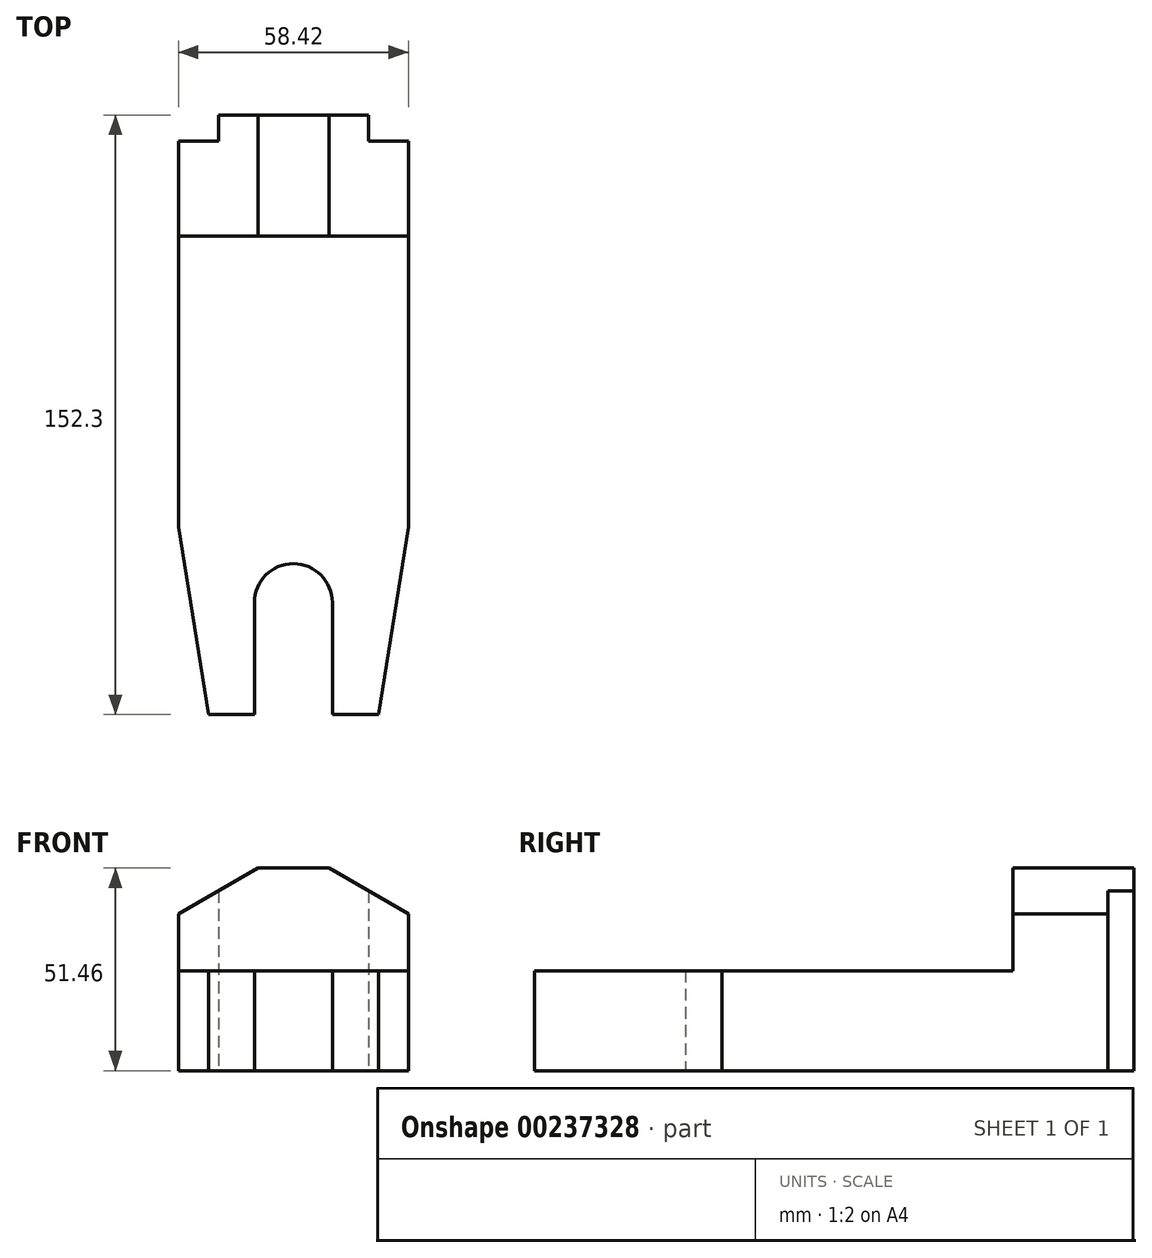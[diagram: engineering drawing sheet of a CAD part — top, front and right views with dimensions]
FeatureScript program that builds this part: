
annotation { "Feature Type Name" : "Feature", "Feature Type Description" : "" }
export const myFeature = defineFeature(function(context is Context, id is Id, definition is map)
    precondition{}
    {
        {
            var Q0;
            Q0=qCreatedBy(makeId("Top.planeOp"),FACE);
            var sketch = newSketch(context, id + "F0", { "sketchPlane" : qUnion([Q0])});
            skLineSegment(sketch, "E0.bottom", {"start": v(-30.66, 87.43) * mm, "end": v(27.76, 87.43) * mm});
            skLineSegment(sketch, "E0.top", {"start": v(8.46, -64.87) * mm, "end": v(20.14, -64.87) * mm});
            skLineSegment(sketch, "E0.left", {"start": v(-30.66, 87.43) * mm, "end": v(-30.66, -17.21) * mm});
            skLineSegment(sketch, "E0.right", {"start": v(27.76, 87.43) * mm, "end": v(27.76, -17.21) * mm});
            skLineSegment(sketch, "E1", {"start": v(-30.66, -17.21) * mm, "end": v(-23.04, -64.87) * mm});
            skLineSegment(sketch, "E2", {"start": v(27.76, -17.21) * mm, "end": v(20.14, -64.87) * mm});
            skLineSegment(sketch, "E3", {"start": v(8.46, -64.87) * mm, "end": v(8.46, -36.42) * mm});
            skLineSegment(sketch, "E4", {"start": v(-11.36, -64.87) * mm, "end": v(-11.36, -36.42) * mm});
            skArc(sketch, "E5", {"start": v(8.46, -36.42) * mm, "mid": v(-1.45, -26.51) * mm, "end": v(-11.36, -36.42) * mm});
            skLineSegment(sketch, "E6", {"start": v(-23.04, -64.87) * mm, "end": v(-11.36, -64.87) * mm});
            skSolve(sketch);
        }
        {
            var Q0;
            Q0 = qSketchRegion(id + "F0", true);
            extrude(context, id + "F1", {"entities" : qUnion([Q0]), "depth" : 25.4 * mm});
        }
        {
            var Q0;
            Q0=makeQuery(id+"F1.opExtrude","SWEPT_FACE",FACE,{"disambiguationData":[OSD([sQuery(id+"F0.wireOp",EDGE,"E0.bottom")])]});
            var sketch = newSketch(context, id + "F2", { "sketchPlane" : qUnion([Q0])});
            skLineSegment(sketch, "E7", {"start": v(-7.58, 51.46) * mm, "end": v(-27.76, 39.8) * mm});
            skLineSegment(sketch, "E8", {"start": v(-7.58, 51.46) * mm, "end": v(10.48, 51.46) * mm});
            skLineSegment(sketch, "E9", {"start": v(10.48, 51.46) * mm, "end": v(30.66, 39.8) * mm});
            skLineSegment(sketch, "E10", {"start": v(30.66, 25.4) * mm, "end": v(30.66, 39.8) * mm});
            skLineSegment(sketch, "E11", {"start": v(30.66, 25.4) * mm, "end": v(-27.76, 25.4) * mm});
            skLineSegment(sketch, "E12", {"start": v(-27.76, 25.4) * mm, "end": v(-27.76, 39.8) * mm});
            skSolve(sketch);
        }
        {
            var Q0;
            Q0 = qSketchRegion(id + "F2", true);
            extrude(context, id + "F3", {"entities" : qUnion([Q0]), "operationType" : NewBodyOperationType.ADD, "oppositeDirection" : true, "depth" : 30.73 * mm});
        }
        {
            var Q0;
            Q0=makeQuery(id+"F1.opExtrude","CAP_FACE",FACE,{"disambiguationData":[OSD([sQuery(id+"F0.wireOp",EDGE,"E0.bottom"),sQuery(id+"F0.wireOp",EDGE,"E0.top"),sQuery(id+"F0.wireOp",EDGE,"E0.left"),sQuery(id+"F0.wireOp",EDGE,"E0.right"),sQuery(id+"F0.wireOp",EDGE,"E1"),sQuery(id+"F0.wireOp",EDGE,"E2"),sQuery(id+"F0.wireOp",EDGE,"E3"),sQuery(id+"F0.wireOp",EDGE,"E4"),sQuery(id+"F0.wireOp",EDGE,"E5"),sQuery(id+"F0.wireOp",EDGE,"E6")])],"isStart":true});
            var sketch = newSketch(context, id + "F4", { "sketchPlane" : qUnion([Q0])});
            skLineSegment(sketch, "E13", {"start": v(-30.66, -87.43) * mm, "end": v(-30.66, -80.83) * mm});
            skLineSegment(sketch, "E14", {"start": v(-30.66, -80.83) * mm, "end": v(-20.5, -80.83) * mm});
            skLineSegment(sketch, "E15", {"start": v(-20.5, -80.83) * mm, "end": v(-20.5, -87.43) * mm});
            skSolve(sketch);
        }
        {
            var Q0;
            Q0 = qSketchRegion(id + "F4", true);
            var Q1;
            {var subQ0=sQuery(id+"F4.wireOp",EDGE,"E13");Q1=makeQuery(id+"F4.imprint","IMPRINT",FACE,{"disambiguationData":[TD([[makeQuery(id+"F4.imprint","IMPRINT",EDGE,{"derivedFrom":subQ0}),-1.0]])]});}
            extrude(context, id + "F5", {"entities" : qUnion([Q0, Q1]), "operationType" : NewBodyOperationType.REMOVE, "endBound" : BoundingType.THROUGH_ALL, "oppositeDirection" : true, "depth" : 25.4 * mm});
        }
        {
            var Q0;
            Q0=makeQuery(id+"F1.opExtrude","CAP_FACE",FACE,{"disambiguationData":[OSD([sQuery(id+"F0.wireOp",EDGE,"E0.bottom"),sQuery(id+"F0.wireOp",EDGE,"E0.top"),sQuery(id+"F0.wireOp",EDGE,"E0.left"),sQuery(id+"F0.wireOp",EDGE,"E0.right"),sQuery(id+"F0.wireOp",EDGE,"E1"),sQuery(id+"F0.wireOp",EDGE,"E2"),sQuery(id+"F0.wireOp",EDGE,"E3"),sQuery(id+"F0.wireOp",EDGE,"E4"),sQuery(id+"F0.wireOp",EDGE,"E5"),sQuery(id+"F0.wireOp",EDGE,"E6")])],"isStart":true});
            var sketch = newSketch(context, id + "F6", { "sketchPlane" : qUnion([Q0])});
            skLineSegment(sketch, "E16", {"start": v(27.76, -87.43) * mm, "end": v(27.76, -80.83) * mm});
            skLineSegment(sketch, "E17", {"start": v(27.76, -80.83) * mm, "end": v(17.6, -80.83) * mm});
            skLineSegment(sketch, "E18", {"start": v(17.6, -80.83) * mm, "end": v(17.6, -87.43) * mm});
            skSolve(sketch);
        }
        {
            var Q0;
            Q0 = qSketchRegion(id + "F6", true);
            var Q1;
            {var subQ0=sQuery(id+"F6.wireOp",EDGE,"E16");Q1=makeQuery(id+"F6.imprint","IMPRINT",FACE,{"disambiguationData":[TD([[makeQuery(id+"F6.imprint","IMPRINT",EDGE,{"derivedFrom":subQ0}),1.0]])]});}
            extrude(context, id + "F7", {"entities" : qUnion([Q0, Q1]), "operationType" : NewBodyOperationType.REMOVE, "endBound" : BoundingType.THROUGH_ALL, "oppositeDirection" : true, "depth" : 25.4 * mm});
        }
    });
